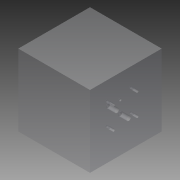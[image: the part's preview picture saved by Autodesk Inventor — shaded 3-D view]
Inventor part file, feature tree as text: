
AUTODESK INVENTOR PART (.ipt)
format: ipt  version: 2014 (Build 180170000, 170)  size: 186,880 bytes
history: native  units: mm
features: other x48, extrude x13, sketch x13
ambient origin geometry x8: Origin, YZ Plane, XZ Plane, XY Plane, X Axis, Y Axis, Z Axis, Center Point
bodies: 实体1 (feature_tree)
feature tree (74):
  extrude  "拉伸1"  Depth=101.0mm
  other  "UCS1"
  other  "UCS2"
  other  "UCS3"
  other  "UCS4"
  other  "UCS5"
  other  "UCS6"
  extrude  "拉伸2"  Depth=125.0mm
  extrude  "拉伸3"  Depth=6.8mm
  extrude  "拉伸4"  Depth=41.3mm
  extrude  "拉伸5"  TaperAngle=0.0deg  [1 undecoded]
  extrude  "拉伸6"  Depth=82.6mm
  extrude  "拉伸7"  TaperAngle=0.0deg  [1 undecoded]
  extrude  "拉伸8"  Depth=4.0mm TaperAngle=0.0deg
  extrude  "拉伸9"  Depth=4.0mm
  extrude  "拉伸10"  Depth=16.0mm TaperAngle=0.0deg
  extrude  "拉伸11"  Depth=16.0mm
  extrude  "拉伸12"  Depth=16.0mm
  extrude  "拉伸13"  Depth=16.0mm
  sketch  "草图1"  dims[d0=250.0mm d1=0.0mm]
  sketch  "草图2"  dims[d2=0.0mm d3=0.0mm d4=0.0mm d5=0.0mm d6=0.0mm d7=0.0mm]
  sketch  "草图3"  dims[d8=0.0mm d9=0.0mm d10=0.0mm d11=0.0mm d12=0.0mm d13=0.0mm]
  sketch  "草图4"  dims[d14=0.0mm d15=0.0mm d16=0.0mm d17=0.0mm d18=0.0mm d19=0.0mm]
  sketch  "草图5"  dims[d20=0.0mm d21=0.0mm d22=0.0mm d23=0.0mm d24=0.0mm d25=0.0mm]
  sketch  "草图6"  dims[d26=0.0mm d27=0.0mm d28=0.0mm d29=0.0mm d30=0.0mm d31=0.0mm]
  sketch  "草图7"  dims[d32=0.0mm d33=0.0mm d34=0.0mm d35=0.0mm d36=0.0mm d37=0.0mm d38=101.0mm]
  sketch  "草图8"  dims[d39=95.0mm d40=125.0mm]
  sketch  "草图9"  dims[d41=124.0mm d44=6.8mm]
  sketch  "草图10"  dims[d45=38.1mm d46=41.3mm]
  sketch  "草图11"  dims[d47=76.2mm d48=0.0mm]
  sketch  "草图12"  dims[d49=76.2mm d50=82.6mm]
  sketch  "草图13"  dims[d51=82.6mm d52=0.0mm d53=26.0mm d54=0.0mm d55=8.0mm d56=16.0mm d57=0.0mm d58=16.0mm d59=-10.297443mm d60=16.0mm d61=-10.297443mm d62=16.0mm d63=-10.297443mm d64=16.0mm d65=-10.297443mm d66=14.7mm d67=54.0mm d68=11.1mm d69=31.0mm d70=0.0mm d71=31.0mm d72=-10.297443mm d73=14.7mm d74=52.4mm d75=9.5mm d76=30.0mm d77=0.0mm d78=30.0mm d79=-10.297443mm d80=7.5mm d81=23.8mm d82=79.4mm d83=4.0mm d84=0.0mm d85=4.0mm d86=-10.297443mm]
  other  "UCS1: YZ 平面"
  other  "UCS1: XZ 平面"
  other  "UCS1: XY 平面"
  other  "UCS1: X 轴"
  other  "UCS1: Y 轴"
  other  "UCS1: Z 轴"
  other  "UCS1: 原点"
  other  "UCS2: YZ 平面"
  other  "UCS2: XZ 平面"
  other  "UCS2: XY 平面"
  other  "UCS2: X 轴"
  other  "UCS2: Y 轴"
  other  "UCS2: Z 轴"
  other  "UCS2: 原点"
  other  "UCS3: YZ 平面"
  other  "UCS3: XZ 平面"
  other  "UCS3: XY 平面"
  other  "UCS3: X 轴"
  other  "UCS3: Y 轴"
  other  "UCS3: Z 轴"
  other  "UCS3: 原点"
  other  "UCS4: YZ 平面"
  other  "UCS4: XZ 平面"
  other  "UCS4: XY 平面"
  other  "UCS4: X 轴"
  other  "UCS4: Y 轴"
  other  "UCS4: Z 轴"
  other  "UCS4: 原点"
  other  "UCS5: YZ 平面"
  other  "UCS5: XZ 平面"
  other  "UCS5: XY 平面"
  other  "UCS5: X 轴"
  other  "UCS5: Y 轴"
  other  "UCS5: Z 轴"
  other  "UCS5: 原点"
  other  "UCS6: YZ 平面"
  other  "UCS6: XZ 平面"
  other  "UCS6: XY 平面"
  other  "UCS6: X 轴"
  other  "UCS6: Y 轴"
  other  "UCS6: Z 轴"
  other  "UCS6: 原点"
note: 2 required parameter values undecoded (feature->parameter linkage not recoverable at this tier; creation-order binding heuristic only, values carry confidence <= 0.55)
